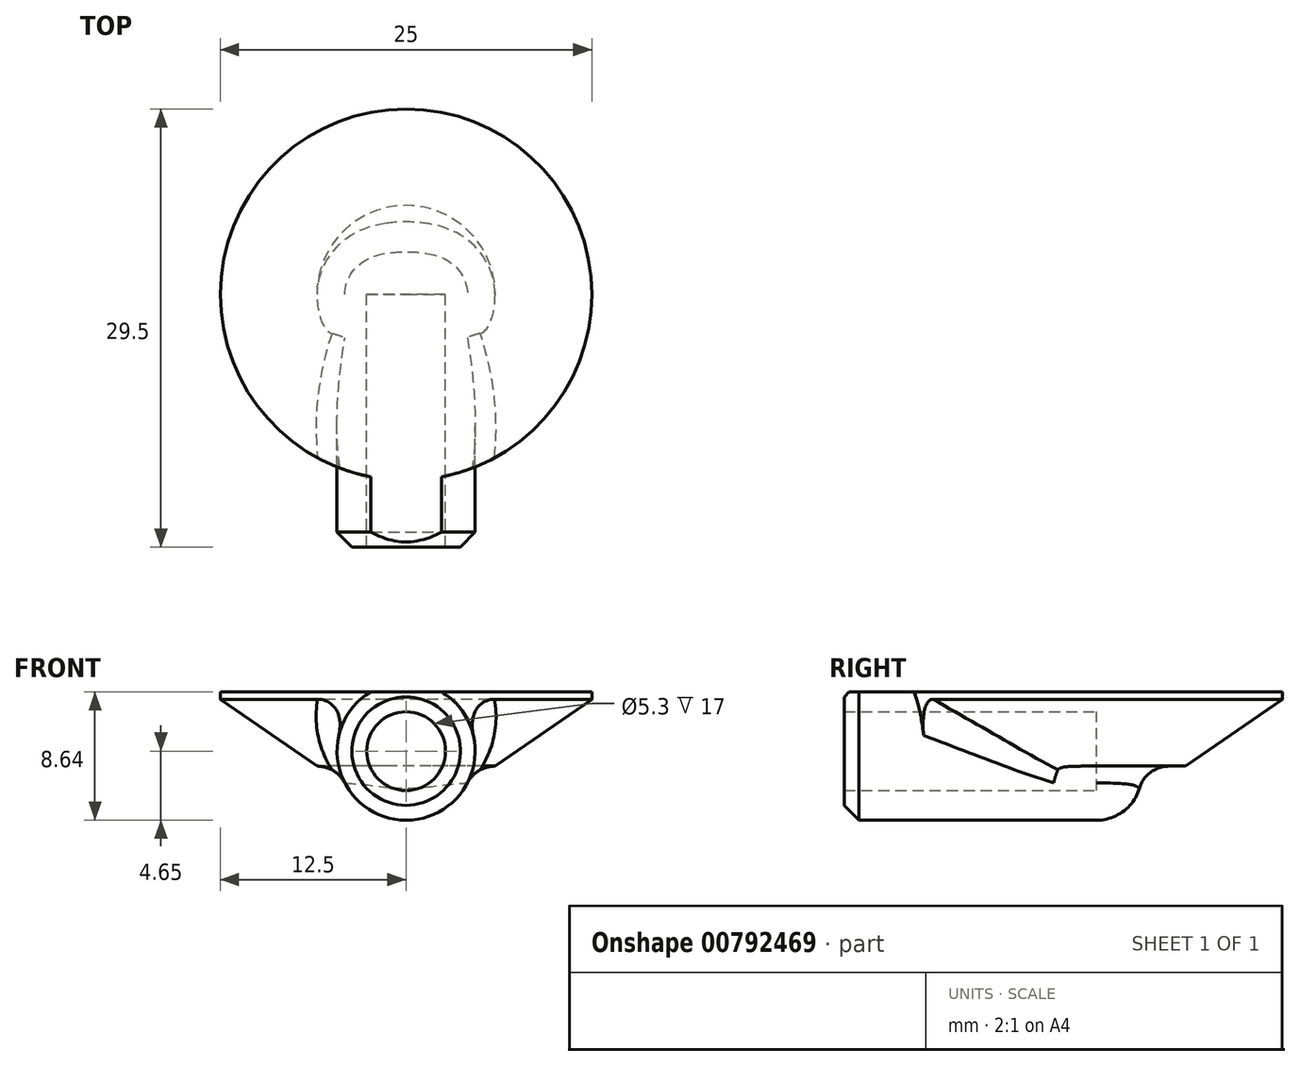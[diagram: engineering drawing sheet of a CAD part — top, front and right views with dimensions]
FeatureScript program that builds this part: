
annotation { "Feature Type Name" : "Feature", "Feature Type Description" : "" }
export const myFeature = defineFeature(function(context is Context, id is Id, definition is map)
    precondition{}
    {
        {
            var Q0;
            Q0=qCreatedBy(makeId("Top.planeOp"),FACE);
            var sketch = newSketch(context, id + "F0", { "sketchPlane" : qUnion([Q0])});
            skCircle(sketch, "E0", {"center": v(0, 0) * mm, "radius": 12.5 * mm});
            skSolve(sketch);
        }
        {
            var Q0;
            Q0 = qSketchRegion(id + "F0", true);
            extrude(context, id + "F1", {"entities" : qUnion([Q0]), "oppositeDirection" : true, "depth" : 5 * mm, "offsetDistance" : 25 * mm});
        }
        {
            var Q0;
            Q0=qCreatedBy(makeId("Front.planeOp"),FACE);
            var sketch = newSketch(context, id + "F2", { "sketchPlane" : qUnion([Q0])});
            skArc(sketch, "E1.0", {"start": v(-2.39, 0) * mm, "mid": v(0, -8.64) * mm, "end": v(2.39, 0) * mm});
            skLineSegment(sketch, "E2", {"start": v(-5.7, 0) * mm, "end": v(6.55, 0) * mm});
            skSolve(sketch);
        }
        {
            var Q0;
            {var subQ0=sQuery(id+"F0.wireOp",EDGE,"E0");Q0=makeQuery(id+"F4.boolean.opBoolean","SPLIT",EDGE,{"disambiguationData":[TD([makeQuery(id+"F4.opExtrude","SWEPT_FACE",FACE,{"disambiguationData":[OSD([sQuery(id+"F2.wireOp",EDGE,"E1.0")])]})])],"derivedFrom":makeQuery(id+"F1.opExtrude","CAP_EDGE",EDGE,{"disambiguationData":[OSD([subQ0])],"isStart":false})});}
            chamfer(context, id + "F3", {"entities" : qUnion([Q0]), "chamferType" : ChamferType.TWO_OFFSETS, "width1" : 4.5 * mm, "oppositeDirection" : false, "width2" : 6.5 * mm, "tangentPropagation" : true});
        }
        {
            var Q0;
            {var subQ0=sQuery(id+"F2.wireOp",EDGE,"E1.0");Q0=makeQuery(id+"F2.imprint","IMPRINT",FACE,{"disambiguationData":[TD([[makeQuery(id+"F2.imprint","IMPRINT",EDGE,{"derivedFrom":subQ0}),1.0]])]});}
            var Q1;
            Q1=sQuery(id+"F2.wireOp",EDGE,"E1.0");
            extrude(context, id + "F4", {"entities" : qUnion([Q0]), "operationType" : NewBodyOperationType.ADD, "surfaceEntities" : qUnion([Q1]), "depth" : 17 * mm, "offsetDistance" : 25 * mm, "hasSecondDirection" : true, "secondDirectionOppositeDirection" : true, "secondDirectionDepth" : 3 * mm});
        }
        {
            var Q0;
            Q0=qCreatedBy(makeId("Front.planeOp"),FACE);
            var sketch = newSketch(context, id + "F5", { "sketchPlane" : qUnion([Q0])});
            skCircle(sketch, "E3", {"center": v(0, -4) * mm, "radius": 2.65 * mm});
            skSolve(sketch);
        }
        {
            var Q0;
            Q0 = qSketchRegion(id + "F5", true);
            extrude(context, id + "F6", {"entities" : qUnion([Q0]), "operationType" : NewBodyOperationType.REMOVE, "depth" : 25 * mm, "offsetDistance" : 25 * mm});
        }
        {
            var Q0;
            Q0=makeQuery(id+"F4.opExtrude","CAP_EDGE",EDGE,{"disambiguationData":[OSD([sQuery(id+"F2.wireOp",EDGE,"E1.0")])],"isStart":false});
            chamfer(context, id + "F7", {"entities" : qUnion([Q0]), "width" : 1 * mm, "tangentPropagation" : true});
        }
        {
            var Q0;
            Q0=makeQuery(id+"F4.opExtrude","CAP_EDGE",EDGE,{"disambiguationData":[OSD([sQuery(id+"F2.wireOp",EDGE,"E1.0")])],"isStart":true});
            fillet(context, id + "F8", {"entities" : qUnion([Q0]), "radius" : 3 * mm, "tangentPropagation" : true, "allowEdgeOverflow" : false});
        }
        {
            var Q0;
            Q0=makeQuery(id+"F8.opFillet","BLEND_EDGE",EDGE,{"disambiguationData":[OD(1.0)],"blendedFrom":[makeQuery(id+"F4.opExtrude","CAP_EDGE",EDGE,{"disambiguationData":[OSD([sQuery(id+"F2.wireOp",EDGE,"E1.0")])],"isStart":true}),makeQuery(id+"F1.opExtrude","CAP_FACE",FACE,{"disambiguationData":[OSD([sQuery(id+"F0.wireOp",EDGE,"E0")])],"isStart":false})],"blendedInto":[makeQuery(id+"F1.opExtrude","CAP_FACE",FACE,{"disambiguationData":[OSD([sQuery(id+"F0.wireOp",EDGE,"E0")])],"isStart":false})]});
            var Q1;
            Q1=makeQuery(id+"F4.boolean.opBoolean","INTERSECT",EDGE,{"derivedFrom":[makeQuery(id+"F1.opExtrude","CAP_FACE",FACE,{"disambiguationData":[OSD([sQuery(id+"F0.wireOp",EDGE,"E0")])],"isStart":false}),makeQuery(id+"F4.opExtrude","CAP_FACE",FACE,{"disambiguationData":[OSD([sQuery(id+"F2.wireOp",EDGE,"E1.0"),sQuery(id+"F2.wireOp",EDGE,"E2")])],"isStart":true})]});
            var Q2;
            Q2=makeQuery(id+"F8.opFillet","BLEND_EDGE",EDGE,{"disambiguationData":[OD(0.0)],"blendedFrom":[makeQuery(id+"F4.opExtrude","CAP_EDGE",EDGE,{"disambiguationData":[OSD([sQuery(id+"F2.wireOp",EDGE,"E1.0")])],"isStart":true}),makeQuery(id+"F1.opExtrude","CAP_FACE",FACE,{"disambiguationData":[OSD([sQuery(id+"F0.wireOp",EDGE,"E0")])],"isStart":false})],"blendedInto":[makeQuery(id+"F1.opExtrude","CAP_FACE",FACE,{"disambiguationData":[OSD([sQuery(id+"F0.wireOp",EDGE,"E0")])],"isStart":false})]});
            var Q3;
            Q3=makeQuery(id+"F4.boolean.opBoolean","INTERSECT",EDGE,{"disambiguationData":[OD(0.0)],"derivedFrom":[makeQuery(id+"F1.opExtrude","CAP_FACE",FACE,{"disambiguationData":[OSD([sQuery(id+"F0.wireOp",EDGE,"E0")])],"isStart":false}),makeQuery(id+"F4.opExtrude","SWEPT_FACE",FACE,{"disambiguationData":[OSD([sQuery(id+"F2.wireOp",EDGE,"E1.0")])]})]});
            var Q4;
            Q4=makeQuery(id+"F4.boolean.opBoolean","INTERSECT",EDGE,{"disambiguationData":[OD(0.0)],"derivedFrom":[makeQuery(id+"F3.opChamfer","BLEND_FACE",FACE,{"disambiguationData":[OSD([sQuery(id+"F0.wireOp",EDGE,"E0")])]}),makeQuery(id+"F4.opExtrude","SWEPT_FACE",FACE,{"disambiguationData":[OSD([sQuery(id+"F2.wireOp",EDGE,"E1.0")])]})]});
            var Q5;
            Q5=makeQuery(id+"F4.boolean.opBoolean","INTERSECT",EDGE,{"disambiguationData":[OD(1.0)],"derivedFrom":[makeQuery(id+"F1.opExtrude","CAP_FACE",FACE,{"disambiguationData":[OSD([sQuery(id+"F0.wireOp",EDGE,"E0")])],"isStart":false}),makeQuery(id+"F4.opExtrude","SWEPT_FACE",FACE,{"disambiguationData":[OSD([sQuery(id+"F2.wireOp",EDGE,"E1.0")])]})]});
            var Q6;
            Q6=makeQuery(id+"F4.boolean.opBoolean","INTERSECT",EDGE,{"disambiguationData":[OD(1.0)],"derivedFrom":[makeQuery(id+"F3.opChamfer","BLEND_FACE",FACE,{"disambiguationData":[OSD([sQuery(id+"F0.wireOp",EDGE,"E0")])]}),makeQuery(id+"F4.opExtrude","SWEPT_FACE",FACE,{"disambiguationData":[OSD([sQuery(id+"F2.wireOp",EDGE,"E1.0")])]})]});
            fillet(context, id + "F9", {"entities" : qUnion([Q0, Q1, Q2, Q3, Q4, Q5, Q6]), "radius" : 2.1 * mm, "tangentPropagation" : true, "allowEdgeOverflow" : false});
        }
    });
